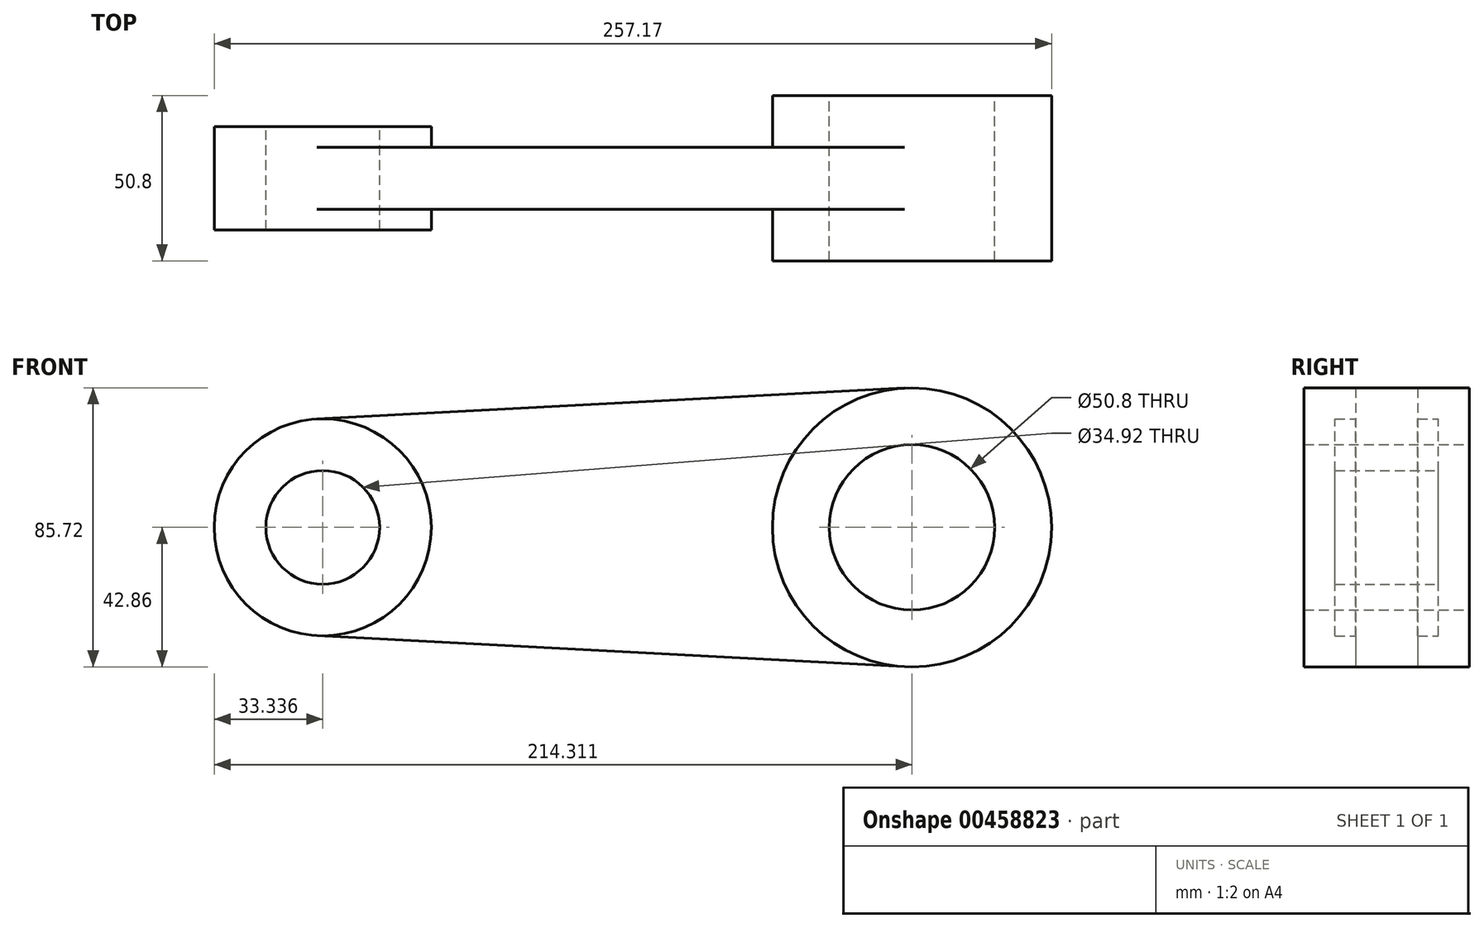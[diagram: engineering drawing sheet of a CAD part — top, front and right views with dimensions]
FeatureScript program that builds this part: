
annotation { "Feature Type Name" : "Feature", "Feature Type Description" : "" }
export const myFeature = defineFeature(function(context is Context, id is Id, definition is map)
    precondition{}
    {
        {
            var Q0;
            Q0=qCreatedBy(makeId("Front.planeOp"),FACE);
            var sketch = newSketch(context, id + "F0", { "sketchPlane" : qUnion([Q0])});
            skCircle(sketch, "E0", {"center": v(-143.71, 0) * mm, "radius": 33.34 * mm});
            skCircle(sketch, "E1", {"center": v(-143.71, 0) * mm, "radius": 17.46 * mm});
            skCircle(sketch, "E2", {"center": v(37.26, 0) * mm, "radius": 42.86 * mm});
            skCircle(sketch, "E3", {"center": v(37.26, 0) * mm, "radius": 25.4 * mm});
            skLineSegment(sketch, "E4", {"start": v(-145.47, -33.3) * mm, "end": v(35, -42.8) * mm});
            skLineSegment(sketch, "E5", {"start": v(35, 42.8) * mm, "end": v(-145.47, 33.3) * mm});
            skSolve(sketch);
        }
        {
            var Q0;
            Q0=qSketchRegion(id+"F0",true);
            extrude(context, id + "F1", {"entities" : qUnion([Q0]), "depth" : 19.05 * mm, "symmetric" : true});
        }
        {
            var Q0;
            Q0=makeQuery(id+"F0.imprint","IMPRINT",FACE,{"disambiguationData":[TD([[makeQuery(id+"F0.imprint","IMPRINT",EDGE,{"derivedFrom":sQuery(id+"F0.wireOp",EDGE,"E3")}),-1.0]])]});
            extrude(context, id + "F2", {"entities" : qUnion([Q0]), "operationType" : NewBodyOperationType.ADD, "depth" : 50.8 * mm, "symmetric" : true});
        }
        {
            var Q0;
            Q0=makeQuery(id+"F0.imprint","IMPRINT",FACE,{"disambiguationData":[TD([[makeQuery(id+"F0.imprint","IMPRINT",EDGE,{"derivedFrom":sQuery(id+"F0.wireOp",EDGE,"E1")}),-1.0]])]});
            extrude(context, id + "F3", {"entities" : qUnion([Q0]), "operationType" : NewBodyOperationType.ADD, "depth" : 31.75 * mm, "symmetric" : true});
        }
    });
